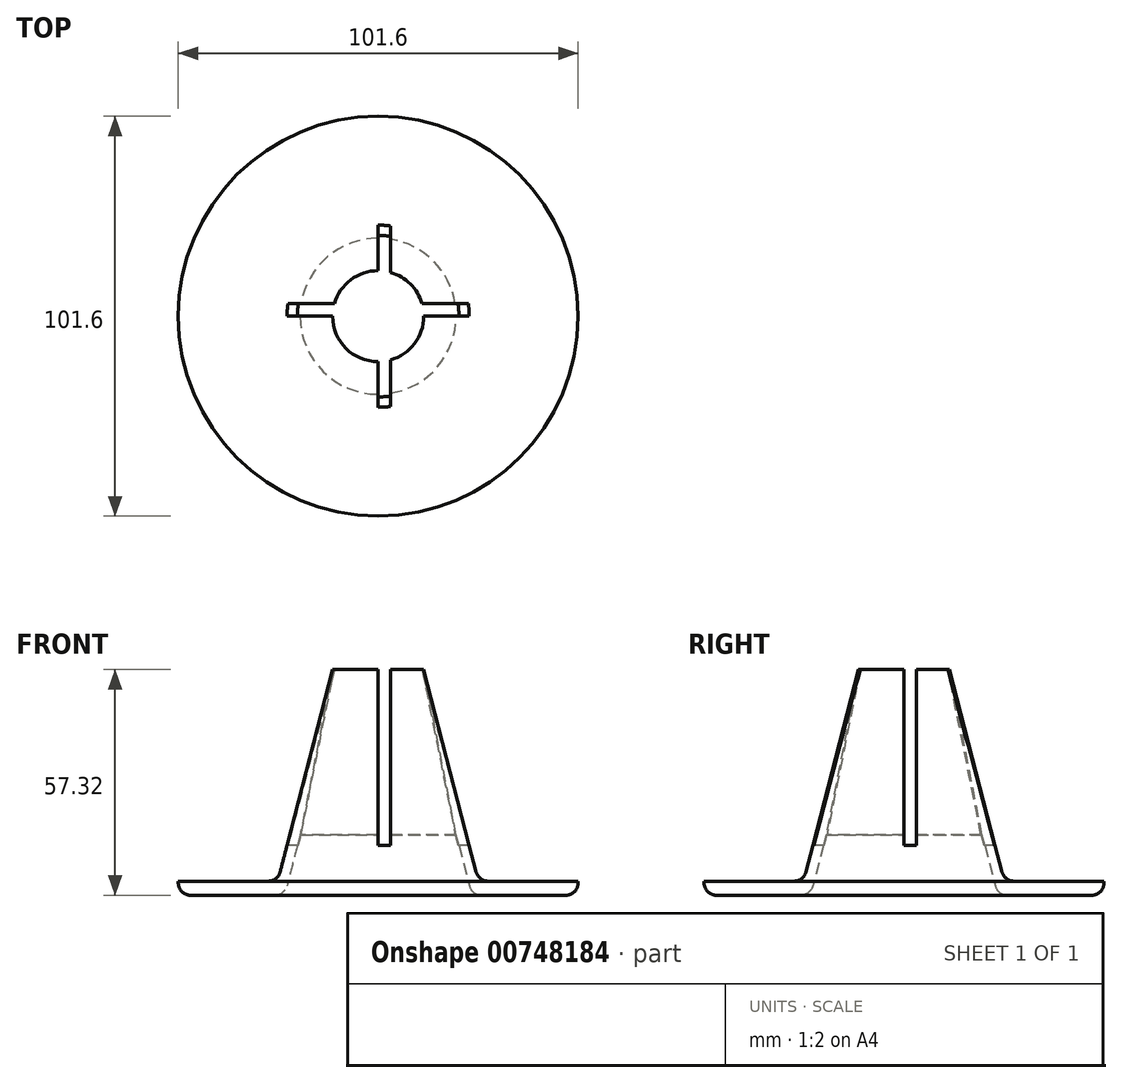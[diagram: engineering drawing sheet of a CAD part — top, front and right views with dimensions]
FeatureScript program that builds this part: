
annotation { "Feature Type Name" : "Feature", "Feature Type Description" : "" }
export const myFeature = defineFeature(function(context is Context, id is Id, definition is map)
    precondition{}
    {
        {
            var Q0;
            Q0=qCreatedBy(makeId("Front.planeOp"),FACE);
            var sketch = newSketch(context, id + "F0", { "sketchPlane" : qUnion([Q0])});
            skLineSegment(sketch, "E0.bottom", {"start": v(23.81, 0) * mm, "end": v(50.8, 0) * mm});
            skLineSegment(sketch, "E0.top", {"start": v(23.81, 3.57) * mm, "end": v(50.8, 3.57) * mm});
            skLineSegment(sketch, "E0.left", {"start": v(23.81, 0) * mm, "end": v(23.81, 3.57) * mm});
            skLineSegment(sketch, "E0.right", {"start": v(50.8, 0) * mm, "end": v(50.8, 3.57) * mm});
            skLineSegment(sketch, "E1.bottom", {"start": v(50.8, 3.57) * mm, "end": v(47.63, 3.57) * mm});
            skLineSegment(sketch, "E1.top", {"start": v(50.8, 41.67) * mm, "end": v(47.63, 41.67) * mm});
            skLineSegment(sketch, "E1.left", {"start": v(50.8, 3.57) * mm, "end": v(50.8, 41.67) * mm});
            skLineSegment(sketch, "E1.right", {"start": v(47.63, 3.57) * mm, "end": v(47.63, 41.67) * mm});
            skLineSegment(sketch, "E2", {"start": v(23.81, 0) * mm, "end": v(7.13, 64.3) * mm});
            skLineSegment(sketch, "E3", {"start": v(7.13, 64.3) * mm, "end": v(9.6, 64.93) * mm});
            skLineSegment(sketch, "E4", {"start": v(9.6, 64.93) * mm, "end": v(25.5, 3.57) * mm});
            skSolve(sketch);
        }
        {
            var Q0;
            Q0=qCreatedBy(makeId("Right.planeOp"),FACE);
            var sketch = newSketch(context, id + "F1", { "sketchPlane" : qUnion([Q0])});
            skLineSegment(sketch, "E5", {"start": v(0, 0) * mm, "end": v(0, 76.4) * mm});
            skSolve(sketch);
        }
        {
            var Q0;
            {var subQ0=sQuery(id+"F0.wireOp",EDGE,"E0.left");Q0=makeQuery(id+"F0.imprint","IMPRINT",FACE,{"disambiguationData":[TD([[makeQuery(id+"F0.imprint","IMPRINT",EDGE,{"derivedFrom":subQ0}),1.0]])]});}
            var Q1;
            Q1=makeQuery(id+"F0.imprint","IMPRINT",FACE,{"disambiguationData":[TD([[makeQuery(id+"F0.imprint","IMPRINT",EDGE,{"derivedFrom":sQuery(id+"F0.wireOp",EDGE,"E0.bottom")}),1.0]])]});
            var Q2;
            Q2=makeQuery(id+"F0.imprint","IMPRINT",FACE,{"disambiguationData":[TD([[makeQuery(id+"F0.imprint","IMPRINT",EDGE,{"derivedFrom":sQuery(id+"F0.wireOp",EDGE,"E1.bottom")}),-1.0]])]});
            var Q3;
            Q3=sQuery(id+"F1.wireOp",EDGE,"E5");
            revolve(context, id + "F2", {"surfaceOperationType" : NewSurfaceOperationType.NEW, "entities" : qUnion([Q0, Q1, Q2]), "axis" : qUnion([Q3]), "revolveType" : RevolveType.FULL});
        }
        {
            var Q0;
            Q0=makeQuery(id+"F2.opRevolve","SWEPT_EDGE",EDGE,{"disambiguationData":[OSD([sQuery(id+"F0.wireOp",EDGE,"E0.bottom"),sQuery(id+"F0.wireOp",EDGE,"E0.right")])]});
            var Q1;
            Q1=makeQuery(id+"F2.opRevolve","SWEPT_EDGE",EDGE,{"disambiguationData":[OSD([sQuery(id+"F0.wireOp",EDGE,"E0.bottom"),sQuery(id+"F0.wireOp",EDGE,"E0.left"),sQuery(id+"F0.wireOp",EDGE,"E2")])]});
            var Q2;
            Q2=makeQuery(id+"F2.opRevolve","SWEPT_EDGE",EDGE,{"disambiguationData":[OSD([sQuery(id+"F0.wireOp",EDGE,"E0.top"),sQuery(id+"F0.wireOp",EDGE,"E4")])]});
            var Q3;
            Q3=makeQuery(id+"F2.opRevolve","SWEPT_EDGE",EDGE,{"disambiguationData":[OSD([sQuery(id+"F0.wireOp",EDGE,"E0.top"),sQuery(id+"F0.wireOp",EDGE,"E1.bottom"),sQuery(id+"F0.wireOp",EDGE,"E1.right")])]});
            fillet(context, id + "F3", {"entities" : qUnion([Q0, Q1, Q2, Q3]), "radius" : 3.17 * mm, "tangentPropagation" : true, "allowEdgeOverflow" : false});
        }
        {
            var Q0;
            Q0=qCreatedBy(makeId("Front.planeOp"),FACE);
            var sketch = newSketch(context, id + "F4", { "sketchPlane" : qUnion([Q0])});
            skLineSegment(sketch, "E6.bottom", {"start": v(0, 0) * mm, "end": v(-23.18, 0) * mm});
            skLineSegment(sketch, "E6.top", {"start": v(0, 12.7) * mm, "end": v(-23.18, 12.7) * mm});
            skLineSegment(sketch, "E6.left", {"start": v(0, 0) * mm, "end": v(0, 12.7) * mm});
            skLineSegment(sketch, "E6.right", {"start": v(-23.18, 0) * mm, "end": v(-23.18, 12.7) * mm});
            skLineSegment(sketch, "E7.bottom", {"start": v(0, 12.7) * mm, "end": v(-3.18, 12.7) * mm});
            skLineSegment(sketch, "E7.top", {"start": v(0, 68.38) * mm, "end": v(-3.18, 68.38) * mm});
            skLineSegment(sketch, "E7.left", {"start": v(0, 12.7) * mm, "end": v(0, 68.38) * mm});
            skLineSegment(sketch, "E7.right", {"start": v(-3.18, 12.7) * mm, "end": v(-3.18, 68.38) * mm});
            skLineSegment(sketch, "E8.bottom", {"start": v(0, 12.7) * mm, "end": v(3.17, 12.7) * mm});
            skLineSegment(sketch, "E8.top", {"start": v(0, 68.32) * mm, "end": v(3.17, 68.32) * mm});
            skLineSegment(sketch, "E8.left", {"start": v(0, 12.7) * mm, "end": v(0, 68.32) * mm});
            skLineSegment(sketch, "E8.right", {"start": v(3.17, 12.7) * mm, "end": v(3.17, 68.32) * mm});
            skSolve(sketch);
        }
        {
            var Q0;
            Q0=makeQuery(id+"F4.imprint","IMPRINT",FACE,{"disambiguationData":[TD([[makeQuery(id+"F4.imprint","IMPRINT",EDGE,{"derivedFrom":sQuery(id+"F4.wireOp",EDGE,"E8.bottom")}),1.0]])]});
            var Q1;
            Q1=makeQuery(id+"F4.imprint","IMPRINT",FACE,{"disambiguationData":[TD([[makeQuery(id+"F4.imprint","IMPRINT",EDGE,{"derivedFrom":sQuery(id+"F4.wireOp",EDGE,"E7.bottom")}),-1.0]])]});
            extrude(context, id + "F5", {"entities" : qUnion([Q0, Q1]), "operationType" : NewBodyOperationType.REMOVE, "endBound" : BoundingType.SYMMETRIC, "oppositeDirection" : true, "depth" : 61.47 * mm, "offsetDistance" : 25.4 * mm});
        }
        {
            var Q0;
            Q0=qCreatedBy(makeId("Right.planeOp"),FACE);
            var sketch = newSketch(context, id + "F6", { "sketchPlane" : qUnion([Q0])});
            skLineSegment(sketch, "E9.bottom", {"start": v(0, 0) * mm, "end": v(-23.18, 0) * mm});
            skLineSegment(sketch, "E9.top", {"start": v(0, 12.7) * mm, "end": v(-23.18, 12.7) * mm});
            skLineSegment(sketch, "E9.left", {"start": v(0, 0) * mm, "end": v(0, 12.7) * mm});
            skLineSegment(sketch, "E9.right", {"start": v(-23.18, 0) * mm, "end": v(-23.18, 12.7) * mm});
            skLineSegment(sketch, "E10.bottom", {"start": v(0, 12.7) * mm, "end": v(-3.18, 12.7) * mm});
            skLineSegment(sketch, "E10.top", {"start": v(0, 77.02) * mm, "end": v(-3.18, 77.02) * mm});
            skLineSegment(sketch, "E10.left", {"start": v(0, 12.7) * mm, "end": v(0, 77.02) * mm});
            skLineSegment(sketch, "E10.right", {"start": v(-3.18, 12.7) * mm, "end": v(-3.18, 77.02) * mm});
            skLineSegment(sketch, "E11.bottom", {"start": v(0, 12.7) * mm, "end": v(3.17, 12.7) * mm});
            skLineSegment(sketch, "E11.top", {"start": v(0, 80.21) * mm, "end": v(3.17, 80.21) * mm});
            skLineSegment(sketch, "E11.left", {"start": v(0, 12.7) * mm, "end": v(0, 80.21) * mm});
            skLineSegment(sketch, "E11.right", {"start": v(3.17, 12.7) * mm, "end": v(3.17, 80.21) * mm});
            skSolve(sketch);
        }
        {
            var Q0;
            {var subQ3=sQuery(id+"F6.wireOp",EDGE,"E11.bottom");Q0=makeQuery(id+"F6.imprint","IMPRINT",FACE,{"disambiguationData":[TD([[makeQuery(id+"F6.imprint","IMPRINT",EDGE,{"derivedFrom":subQ3}),1.0]])]});}
            var Q1;
            {var subQ0=sQuery(id+"F6.wireOp",EDGE,"E10.bottom");Q1=makeQuery(id+"F6.imprint","IMPRINT",FACE,{"disambiguationData":[TD([[makeQuery(id+"F6.imprint","IMPRINT",EDGE,{"derivedFrom":subQ0}),-1.0]])]});}
            extrude(context, id + "F7", {"entities" : qUnion([Q0, Q1]), "operationType" : NewBodyOperationType.REMOVE, "endBound" : BoundingType.SYMMETRIC, "depth" : 54.36 * mm, "offsetDistance" : 25.4 * mm});
        }
        {
            var Q0;
            Q0=qCreatedBy(makeId("Top.planeOp"),FACE);
            var sketch = newSketch(context, id + "F8", { "sketchPlane" : qUnion([Q0])});
            skCircle(sketch, "E12", {"center": v(0, 0) * mm, "radius": 11.53 * mm});
            skSolve(sketch);
        }
        {
            var Q0;
            Q0=makeQuery(id+"F8.imprint","IMPRINT",FACE,{"disambiguationData":[TD([[makeQuery(id+"F8.imprint","IMPRINT",EDGE,{"derivedFrom":sQuery(id+"F8.wireOp",EDGE,"E12")}),1.0]])]});
            extrude(context, id + "F9", {"entities" : qUnion([Q0]), "operationType" : NewBodyOperationType.REMOVE, "depth" : 72.14 * mm, "offsetDistance" : 25.4 * mm});
        }
        {
            var Q0;
            Q0=makeQuery(id+"F9.boolean.opBoolean","INTERSECT",EDGE,{"disambiguationData":[OD(3.0)],"derivedFrom":[makeQuery(id+"F2.opRevolve","SWEPT_FACE",FACE,{"disambiguationData":[OSD([sQuery(id+"F0.wireOp",EDGE,"E2")])]}),makeQuery(id+"F9.opExtrude","SWEPT_FACE",FACE,{"disambiguationData":[OSD([sQuery(id+"F8.wireOp",EDGE,"E12")])]})]});
            var Q1;
            Q1=makeQuery(id+"F9.boolean.opBoolean","INTERSECT",EDGE,{"disambiguationData":[OD(1.0)],"derivedFrom":[makeQuery(id+"F2.opRevolve","SWEPT_FACE",FACE,{"disambiguationData":[OSD([sQuery(id+"F0.wireOp",EDGE,"E2")])]}),makeQuery(id+"F9.opExtrude","SWEPT_FACE",FACE,{"disambiguationData":[OSD([sQuery(id+"F8.wireOp",EDGE,"E12")])]})]});
            var Q2;
            Q2=makeQuery(id+"F9.boolean.opBoolean","INTERSECT",EDGE,{"disambiguationData":[OD(2.0)],"derivedFrom":[makeQuery(id+"F2.opRevolve","SWEPT_FACE",FACE,{"disambiguationData":[OSD([sQuery(id+"F0.wireOp",EDGE,"E2")])]}),makeQuery(id+"F9.opExtrude","SWEPT_FACE",FACE,{"disambiguationData":[OSD([sQuery(id+"F8.wireOp",EDGE,"E12")])]})]});
            var Q3;
            Q3=makeQuery(id+"F9.boolean.opBoolean","INTERSECT",EDGE,{"disambiguationData":[OD(0.0)],"derivedFrom":[makeQuery(id+"F2.opRevolve","SWEPT_FACE",FACE,{"disambiguationData":[OSD([sQuery(id+"F0.wireOp",EDGE,"E2")])]}),makeQuery(id+"F9.opExtrude","SWEPT_FACE",FACE,{"disambiguationData":[OSD([sQuery(id+"F8.wireOp",EDGE,"E12")])]})]});
            chamfer(context, id + "F10", {"entities" : qUnion([Q0, Q1, Q2, Q3]), "chamferType" : ChamferType.TWO_OFFSETS, "width1" : 10.16 * mm, "oppositeDirection" : false, "width2" : 33.02 * mm, "tangentPropagation" : true});
        }
    });
